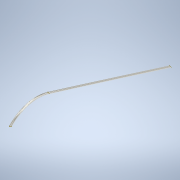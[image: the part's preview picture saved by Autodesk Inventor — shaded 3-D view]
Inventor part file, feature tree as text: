
AUTODESK INVENTOR PART (.ipt)
format: ipt  version: 2022 (Build 260153000, 153)  size: 123,392 bytes
history: native  units: in
note: dims shown in document units (in); Inventor stores cm internally (conversion verified against a paired STEP export)
features: sketch x2, sweep x1
ambient origin geometry x8: Origin, YZ Plane, XZ Plane, XY Plane, X Axis, Y Axis, Z Axis, Center Point
bodies: Solid1 (feature_tree)
feature tree (3):
  sweep  "Sweep1"
  sketch  "Sketch3"  dims[d10=0.001in d12=0.013in]
  sketch  "Sketch4"  dims[d13=0.061in d14=90.0deg d15=0.0in d16=0.0in]
